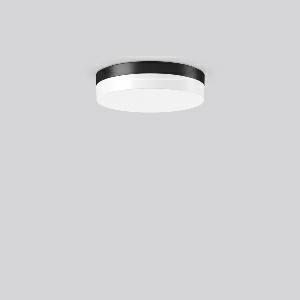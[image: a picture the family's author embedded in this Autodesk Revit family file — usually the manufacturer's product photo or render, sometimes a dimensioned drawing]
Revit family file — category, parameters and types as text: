
# Revit family: flat_slim_round_312673_0031_19_fbec
name_source: partatom
category: Lighting Fixtures
units: mm (PartAtom-declared; Revit-internal decimal feet)

## family parameters
Cut with Voids When Loaded = No
Host = Face
Light Source = No
Part Type = Normal
Room Calculation Point = No
Round Connector Dimension = Use Diameter
Shared = No

## types (1)
- MultiLumen 1 830 (1 x LED Modul 830, 1250 lm, 3000)
    Apparent Load = 13 VA
    CIE Flux Codes = 38 68 89 82 100
    Color Rendering = 80
    Color Temperature = 3000
    Default Elevation = 1800 mm
    Height = 75 mm
    Lamp = 1 x LED Modul 830
    Lamp Light Flux = 1250 lm
    Lamp count = 1
    Length = 300 mm
    Lifetime = 50000 h
    Luminous efficacy = 96 lm/W
    Manufacturer = RZB
    ModVariant = No
    Model = 312673.0031.19
    Mounting Place = Ceiling
    Mounting Type = Surface mounted
    Number of Poles = 1
    OnlyDefault = Yes
    Power Factor = 1
    Product Name = FLAT SLIM round
    Product group = Surface mounted ceiling and wall luminaires
    ProductGroupID = 305
    Protection Class = Protection class I
    Protection Degree = Degree of protection
    RLX_Detail_Level = 1
    RLX_Emergency_Light_Flux = 0 lm
    RLX_Emergency_Type = 0
    RLX_Emergency_Type_DB = No
    RlxData = <blob elided: 18233 chars, md5=adbe5a3b>
    Socket = socket
    Standby Power = 0 W
    System Light Flux = 1250 lm
    System Power = 13 W
    Type Comments = MultiLumen 1 830
    Type Image = 312629.0031.jpg
    URL = http://relux.com
    VarID = multilumen_1_830
    Voltage = 0 V
    Weight = 0.00 kg
    Width = 0 mm  [stored 0 ft]

note: [stored X ft] marks values corroborated as IEEE doubles in the binary element streams (Revit-internal decimal feet)

## geometry (parser evidence)
native form markers: Blend x4, Sweep x12
no freeform markers — native parametric forms only
